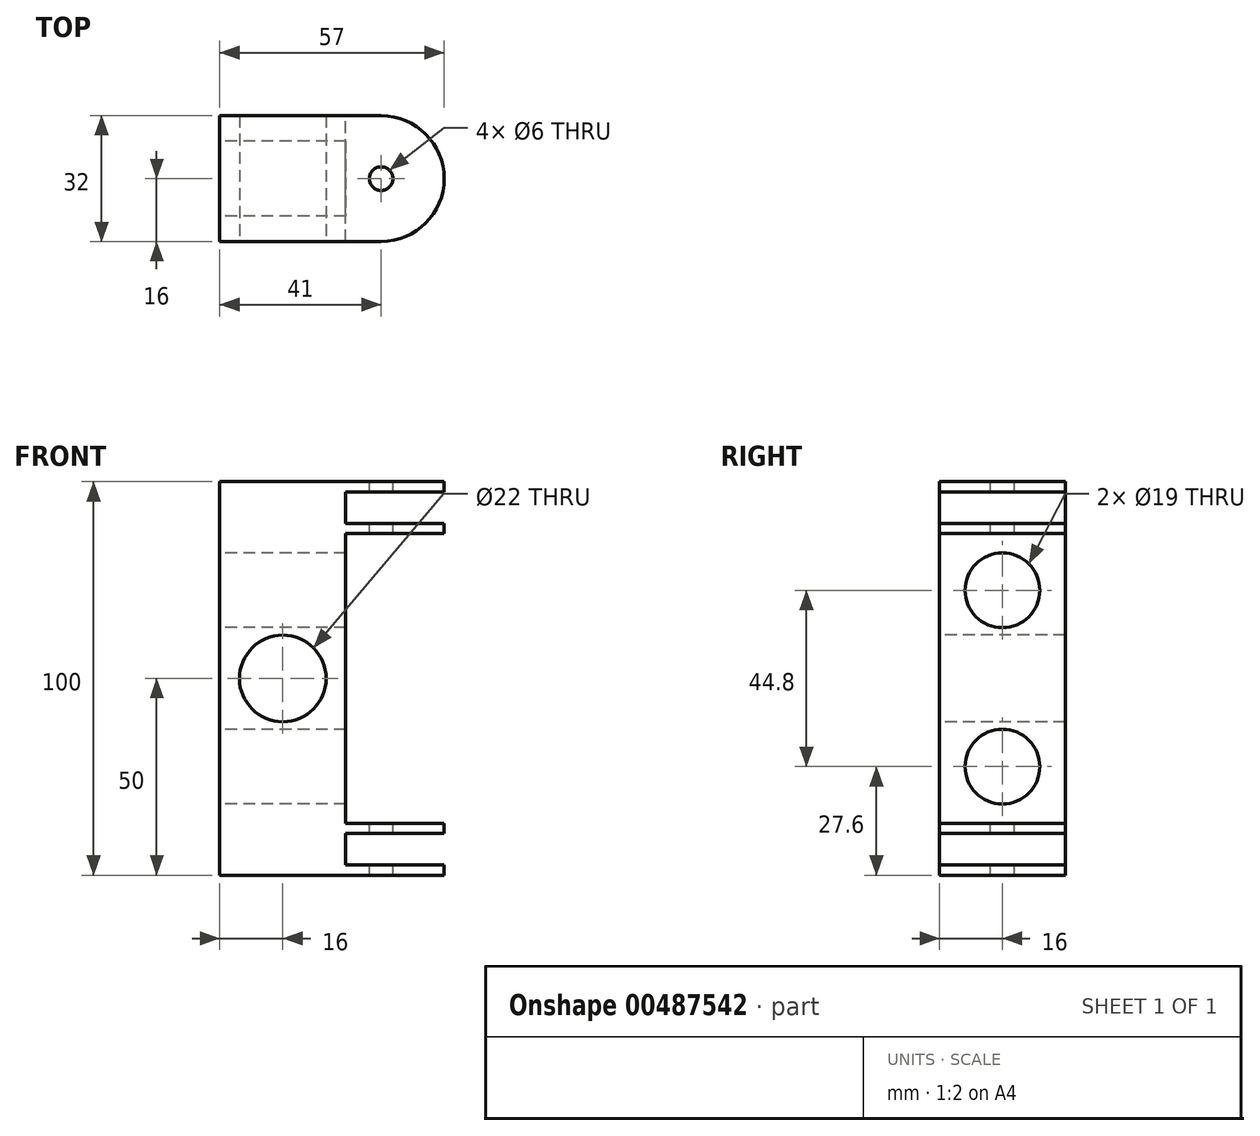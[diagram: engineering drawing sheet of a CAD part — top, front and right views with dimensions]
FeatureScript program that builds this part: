
annotation { "Feature Type Name" : "Feature", "Feature Type Description" : "" }
export const myFeature = defineFeature(function(context is Context, id is Id, definition is map)
    precondition{}
    {
        {
            var Q0;
            Q0=qCreatedBy(makeId("Right.planeOp"),FACE);
            var sketch = newSketch(context, id + "F0", { "sketchPlane" : qUnion([Q0])});
            skLineSegment(sketch, "E0.bottom", {"start": v(16, -50) * mm, "end": v(-16, -50) * mm});
            skLineSegment(sketch, "E0.top", {"start": v(16, 50) * mm, "end": v(-16, 50) * mm});
            skLineSegment(sketch, "E0.left", {"start": v(16, -50) * mm, "end": v(16, 50) * mm});
            skLineSegment(sketch, "E0.right", {"start": v(-16, -50) * mm, "end": v(-16, 50) * mm});
            skPoint(sketch, "E0.middle", {"position": v(0, 0) * mm});
            skCircle(sketch, "E1", {"center": v(0, -22.4) * mm, "radius": 9.5 * mm});
            skCircle(sketch, "E2", {"center": v(0, 22.4) * mm, "radius": 9.5 * mm});
            skSolve(sketch);
        }
        {
            var Q0;
            Q0 = qSketchRegion(id + "F0", true);
            extrude(context, id + "F1", {"entities" : qUnion([Q0]), "depth" : 32 * mm, "offsetDistance" : 25 * mm});
        }
        {
            var Q0;
            Q0=makeQuery(id+"F1.opExtrude","SWEPT_FACE",FACE,{"disambiguationData":[OSD([sQuery(id+"F0.wireOp",EDGE,"E0.right")])]});
            var sketch = newSketch(context, id + "F2", { "sketchPlane" : qUnion([Q0])});
            skCircle(sketch, "E3", {"center": v(16, 0) * mm, "radius": 11 * mm});
            skPoint(sketch, "E3.centerSnap0", {"position": v(16, 50) * mm});
            skSolve(sketch);
        }
        {
            var Q0;
            Q0=makeQuery(id+"F2.imprint","IMPRINT",FACE,{"disambiguationData":[TD([[makeQuery(id+"F2.imprint","IMPRINT",EDGE,{"derivedFrom":sQuery(id+"F2.wireOp",EDGE,"E3")}),1.0]])]});
            extrude(context, id + "F3", {"entities" : qUnion([Q0]), "operationType" : NewBodyOperationType.REMOVE, "endBound" : BoundingType.THROUGH_ALL, "oppositeDirection" : true, "depth" : 25 * mm, "offsetDistance" : 25 * mm});
        }
        {
            var Q0;
            Q0=makeQuery(id+"F1.opExtrude","CAP_FACE",FACE,{"disambiguationData":[OSD([sQuery(id+"F0.wireOp",EDGE,"E0.bottom"),sQuery(id+"F0.wireOp",EDGE,"E0.top"),sQuery(id+"F0.wireOp",EDGE,"E0.left"),sQuery(id+"F0.wireOp",EDGE,"E0.right"),sQuery(id+"F0.wireOp",EDGE,"E1"),sQuery(id+"F0.wireOp",EDGE,"E2")])],"isStart":false});
            var sketch = newSketch(context, id + "F4", { "sketchPlane" : qUnion([Q0])});
            skLineSegment(sketch, "E4.bottom", {"start": v(-16, 50) * mm, "end": v(16, 50) * mm});
            skLineSegment(sketch, "E4.top", {"start": v(-16, 47.4) * mm, "end": v(16, 47.4) * mm});
            skLineSegment(sketch, "E4.left", {"start": v(-16, 50) * mm, "end": v(-16, 47.4) * mm});
            skLineSegment(sketch, "E4.right", {"start": v(16, 50) * mm, "end": v(16, 47.4) * mm});
            skLineSegment(sketch, "E5.bottom", {"start": v(-16, 39.4) * mm, "end": v(16, 39.4) * mm});
            skLineSegment(sketch, "E5.top", {"start": v(-16, 36.8) * mm, "end": v(16, 36.8) * mm});
            skLineSegment(sketch, "E5.left", {"start": v(-16, 39.4) * mm, "end": v(-16, 36.8) * mm});
            skLineSegment(sketch, "E5.right", {"start": v(16, 39.4) * mm, "end": v(16, 36.8) * mm});
            skLineSegment(sketch, "E6.MirrorCS", {"start": v(-16, -36.8) * mm, "end": v(16, -36.8) * mm});
            skLineSegment(sketch, "E7.MirrorCS", {"start": v(-16, -39.4) * mm, "end": v(16, -39.4) * mm});
            skLineSegment(sketch, "E8.MirrorCS", {"start": v(-16, -47.4) * mm, "end": v(16, -47.4) * mm});
            skLineSegment(sketch, "E9.MirrorCS", {"start": v(-16, -50) * mm, "end": v(16, -50) * mm});
            skLineSegment(sketch, "E10.MirrorCS", {"start": v(-16, -39.4) * mm, "end": v(-16, -36.8) * mm});
            skLineSegment(sketch, "E11.MirrorCS", {"start": v(16, -39.4) * mm, "end": v(16, -36.8) * mm});
            skLineSegment(sketch, "E12.MirrorCS", {"start": v(16, -50) * mm, "end": v(16, -47.4) * mm});
            skLineSegment(sketch, "E13.MirrorCS", {"start": v(-16, -50) * mm, "end": v(-16, -47.4) * mm});
            skSolve(sketch);
        }
        {
            var Q0;
            Q0=makeQuery(id+"F4.imprint","IMPRINT",FACE,{"disambiguationData":[TD([[makeQuery(id+"F4.imprint","IMPRINT",EDGE,{"derivedFrom":sQuery(id+"F4.wireOp",EDGE,"E4.bottom")}),1.0]])]});
            var Q1;
            Q1=makeQuery(id+"F4.imprint","IMPRINT",FACE,{"disambiguationData":[TD([[makeQuery(id+"F4.imprint","IMPRINT",EDGE,{"derivedFrom":sQuery(id+"F4.wireOp",EDGE,"E5.bottom")}),-1.0]])]});
            var Q2;
            Q2=makeQuery(id+"F4.imprint","IMPRINT",FACE,{"disambiguationData":[TD([[makeQuery(id+"F4.imprint","IMPRINT",EDGE,{"derivedFrom":sQuery(id+"F4.wireOp",EDGE,"E6.MirrorCS")}),-1.0]])]});
            var Q3;
            Q3=makeQuery(id+"F4.imprint","IMPRINT",FACE,{"disambiguationData":[TD([[makeQuery(id+"F4.imprint","IMPRINT",EDGE,{"derivedFrom":sQuery(id+"F4.wireOp",EDGE,"E8.MirrorCS")}),-1.0]])]});
            extrude(context, id + "F5", {"entities" : qUnion([Q0, Q1, Q2, Q3]), "operationType" : NewBodyOperationType.ADD, "depth" : 25 * mm, "offsetDistance" : 25 * mm});
        }
        {
            var Q0;
            Q0=makeQuery(id+"F5.opExtrude","CAP_EDGE",EDGE,{"disambiguationData":[OSD([sQuery(id+"F4.wireOp",EDGE,"E4.left")])],"isStart":false});
            var Q1;
            Q1=makeQuery(id+"F5.opExtrude","CAP_EDGE",EDGE,{"disambiguationData":[OSD([sQuery(id+"F4.wireOp",EDGE,"E5.left")])],"isStart":false});
            var Q2;
            Q2=makeQuery(id+"F5.opExtrude","CAP_EDGE",EDGE,{"disambiguationData":[OSD([sQuery(id+"F4.wireOp",EDGE,"E5.right")])],"isStart":false});
            var Q3;
            Q3=makeQuery(id+"F5.opExtrude","CAP_EDGE",EDGE,{"disambiguationData":[OSD([sQuery(id+"F4.wireOp",EDGE,"E4.right")])],"isStart":false});
            var Q4;
            Q4=makeQuery(id+"F5.opExtrude","CAP_EDGE",EDGE,{"disambiguationData":[OSD([sQuery(id+"F4.wireOp",EDGE,"E12.MirrorCS")])],"isStart":false});
            var Q5;
            Q5=makeQuery(id+"F5.opExtrude","CAP_EDGE",EDGE,{"disambiguationData":[OSD([sQuery(id+"F4.wireOp",EDGE,"E13.MirrorCS")])],"isStart":false});
            var Q6;
            Q6=makeQuery(id+"F5.opExtrude","CAP_EDGE",EDGE,{"disambiguationData":[OSD([sQuery(id+"F4.wireOp",EDGE,"E10.MirrorCS")])],"isStart":false});
            var Q7;
            Q7=makeQuery(id+"F5.opExtrude","CAP_EDGE",EDGE,{"disambiguationData":[OSD([sQuery(id+"F4.wireOp",EDGE,"E11.MirrorCS")])],"isStart":false});
            fillet(context, id + "F6", {"entities" : qUnion([Q0, Q1, Q2, Q3, Q4, Q5, Q6, Q7]), "radius" : 16 * mm, "tangentPropagation" : true, "allowEdgeOverflow" : false});
        }
        {
            var Q0;
            Q0=makeQuery(id+"F5.boolean.opBoolean","MERGE",FACE,{"derivedFrom":[makeQuery(id+"F1.opExtrude","SWEPT_FACE",FACE,{"disambiguationData":[OSD([sQuery(id+"F0.wireOp",EDGE,"E0.top")])]}),makeQuery(id+"F5.opExtrude","SWEPT_FACE",FACE,{"disambiguationData":[OSD([sQuery(id+"F4.wireOp",EDGE,"E4.bottom")])]})]});
            var sketch = newSketch(context, id + "F7", { "sketchPlane" : qUnion([Q0])});
            skCircle(sketch, "E14", {"center": v(41, 0) * mm, "radius": 3 * mm});
            skSolve(sketch);
        }
        {
            var Q0;
            Q0 = qSketchRegion(id + "F7", true);
            extrude(context, id + "F8", {"entities" : qUnion([Q0]), "operationType" : NewBodyOperationType.REMOVE, "endBound" : BoundingType.THROUGH_ALL, "oppositeDirection" : true, "depth" : 25 * mm, "offsetDistance" : 25 * mm});
        }
    });
